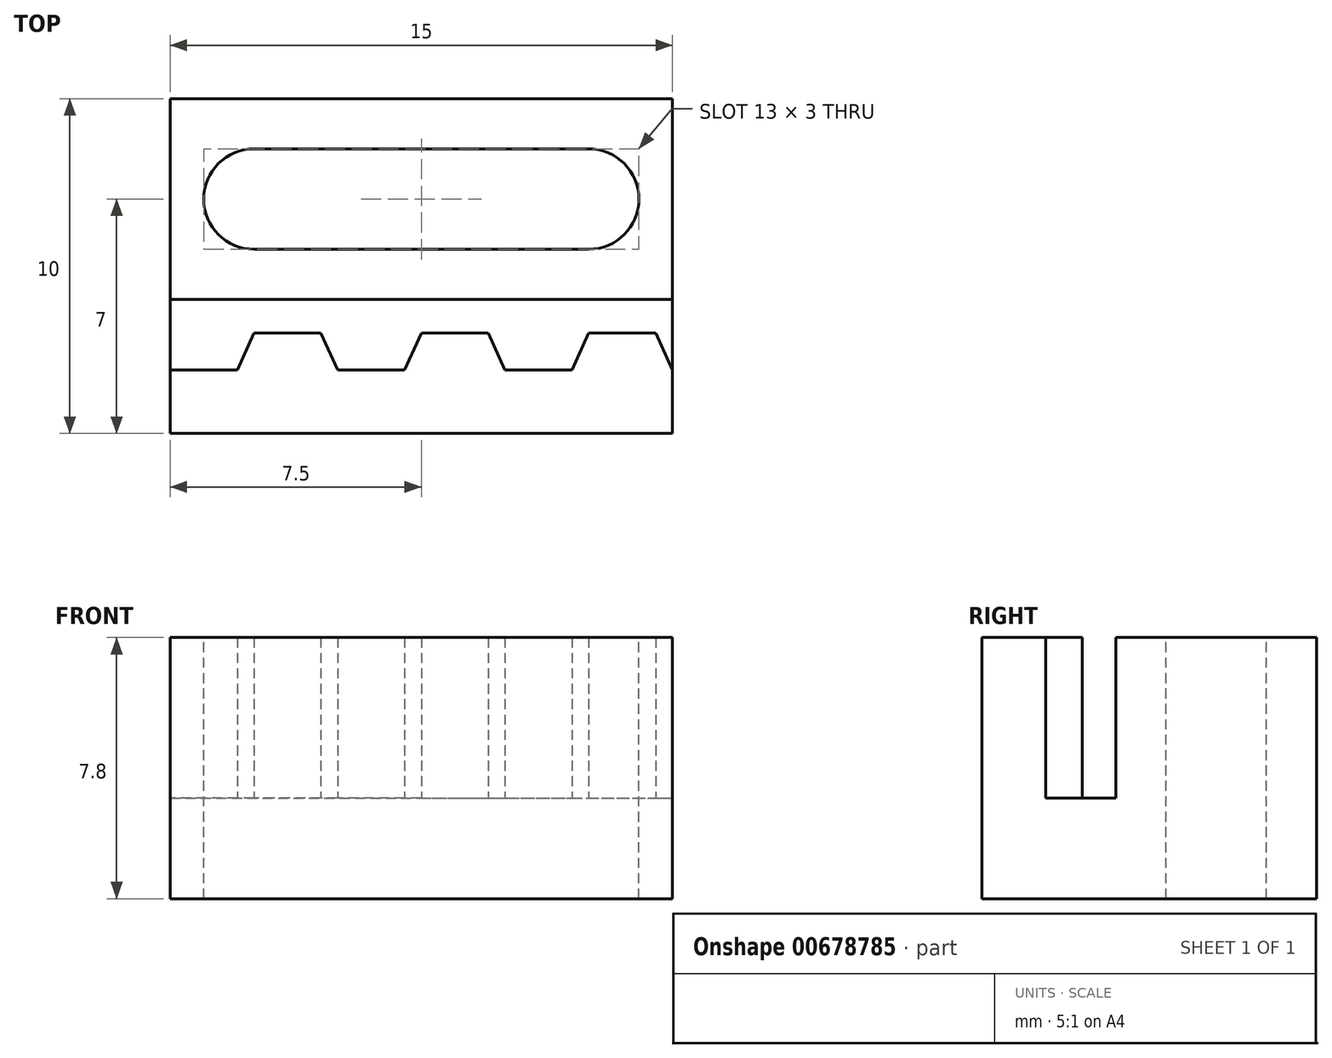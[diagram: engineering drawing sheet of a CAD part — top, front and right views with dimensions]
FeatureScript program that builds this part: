
annotation { "Feature Type Name" : "Feature", "Feature Type Description" : "" }
export const myFeature = defineFeature(function(context is Context, id is Id, definition is map)
    precondition{}
    {
        {
            var Q0;
            Q0=qCreatedBy(makeId("Top.planeOp"),FACE);
            var sketch = newSketch(context, id + "F0", { "sketchPlane" : qUnion([Q0])});
            skLineSegment(sketch, "E0.bottom", {"start": v(7.5, -5) * mm, "end": v(-7.5, -5) * mm});
            skLineSegment(sketch, "E0.top", {"start": v(7.5, 5) * mm, "end": v(-7.5, 5) * mm});
            skLineSegment(sketch, "E0.left", {"start": v(7.5, -5) * mm, "end": v(7.5, 5) * mm});
            skLineSegment(sketch, "E0.right", {"start": v(-7.5, -5) * mm, "end": v(-7.5, 5) * mm});
            skPoint(sketch, "E0.middle", {"position": v(0, 0) * mm});
            skSolve(sketch);
        }
        {
            var Q0;
            Q0 = qSketchRegion(id + "F0", true);
            extrude(context, id + "F1", {"entities" : qUnion([Q0]), "depth" : 3 * mm, "offsetDistance" : 25 * mm});
        }
        {
            var Q0;
            Q0=makeQuery(id+"F1.opExtrude","CAP_FACE",FACE,{"disambiguationData":[OSD([sQuery(id+"F0.wireOp",EDGE,"E0.bottom"),sQuery(id+"F0.wireOp",EDGE,"E0.top"),sQuery(id+"F0.wireOp",EDGE,"E0.left"),sQuery(id+"F0.wireOp",EDGE,"E0.right")])],"isStart":false});
            var sketch = newSketch(context, id + "F2", { "sketchPlane" : qUnion([Q0])});
            skLineSegment(sketch, "E1", {"start": v(0, -2) * mm, "end": v(2, -2) * mm});
            skLineSegment(sketch, "E2", {"start": v(2, -2) * mm, "end": v(2.5, -3.1) * mm});
            skLineSegment(sketch, "E3", {"start": v(2.5, -3.1) * mm, "end": v(4.5, -3.1) * mm});
            skLineSegment(sketch, "E4", {"start": v(4.5, -3.1) * mm, "end": v(5, -2) * mm});
            skLineSegment(sketch, "E5", {"start": v(5, -2) * mm, "end": v(7, -2) * mm});
            skLineSegment(sketch, "E6", {"start": v(7, -2) * mm, "end": v(7.5, -3.1) * mm});
            skLineSegment(sketch, "E7", {"start": v(-7.5, -5) * mm, "end": v(7.5, -5) * mm});
            skLineSegment(sketch, "E8", {"start": v(7.5, -5) * mm, "end": v(7.5, -3.1) * mm});
            skLineSegment(sketch, "E9.bottom", {"start": v(-7.5, -1) * mm, "end": v(7.5, -1) * mm});
            skLineSegment(sketch, "E9.top", {"start": v(-7.5, 5) * mm, "end": v(7.5, 5) * mm});
            skLineSegment(sketch, "E9.left", {"start": v(-7.5, -1) * mm, "end": v(-7.5, 5) * mm});
            skLineSegment(sketch, "E9.right", {"start": v(7.5, -1) * mm, "end": v(7.5, 5) * mm});
            skLineSegment(sketch, "E10", {"start": v(0, -2) * mm, "end": v(-0.5, -3.1) * mm});
            skLineSegment(sketch, "E11", {"start": v(-0.5, -3.1) * mm, "end": v(-2.5, -3.1) * mm});
            skLineSegment(sketch, "E12", {"start": v(-2.5, -3.1) * mm, "end": v(-3, -2) * mm});
            skLineSegment(sketch, "E13", {"start": v(-3, -2) * mm, "end": v(-5, -2) * mm});
            skLineSegment(sketch, "E14", {"start": v(-5, -2) * mm, "end": v(-5.5, -3.1) * mm});
            skLineSegment(sketch, "E15", {"start": v(-5.5, -3.1) * mm, "end": v(-7.5, -3.1) * mm});
            skLineSegment(sketch, "E16", {"start": v(-7.5, -3.1) * mm, "end": v(-7.5, -5) * mm});
            skSolve(sketch);
        }
        {
            var Q0;
            Q0 = qSketchRegion(id + "F2", true);
            extrude(context, id + "F3", {"entities" : qUnion([Q0]), "operationType" : NewBodyOperationType.ADD, "depth" : 4.8 * mm, "offsetDistance" : 25 * mm});
        }
        {
            var Q0;
            Q0=makeQuery(id+"F3.opExtrude","CAP_FACE",FACE,{"disambiguationData":[OSD([sQuery(id+"F2.wireOp",EDGE,"E9.bottom"),sQuery(id+"F2.wireOp",EDGE,"E9.top"),sQuery(id+"F2.wireOp",EDGE,"E9.left"),sQuery(id+"F2.wireOp",EDGE,"E9.right")])],"isStart":false});
            var sketch = newSketch(context, id + "F4", { "sketchPlane" : qUnion([Q0])});
            skArc(sketch, "E17", {"start": v(-5, 3.5) * mm, "mid": v(-6.5, 2) * mm, "end": v(-5, 0.5) * mm});
            skArc(sketch, "E18", {"start": v(5, 0.5) * mm, "mid": v(6.5, 2) * mm, "end": v(5, 3.5) * mm});
            skLineSegment(sketch, "E19", {"start": v(-5, 3.5) * mm, "end": v(5, 3.5) * mm});
            skLineSegment(sketch, "E20", {"start": v(-5, 0.5) * mm, "end": v(5, 0.5) * mm});
            skLineSegment(sketch, "E21", {"start": v(0, -0.58) * mm, "end": v(0, 5.54) * mm, "construction": true});
            skPoint(sketch, "E21.endSnap0", {"position": v(0, 5) * mm});
            skSolve(sketch);
        }
        {
            var Q0;
            Q0 = qSketchRegion(id + "F4", true);
            extrude(context, id + "F5", {"entities" : qUnion([Q0]), "operationType" : NewBodyOperationType.REMOVE, "endBound" : BoundingType.THROUGH_ALL, "oppositeDirection" : true, "depth" : 25 * mm, "offsetDistance" : 25 * mm});
        }
    });
